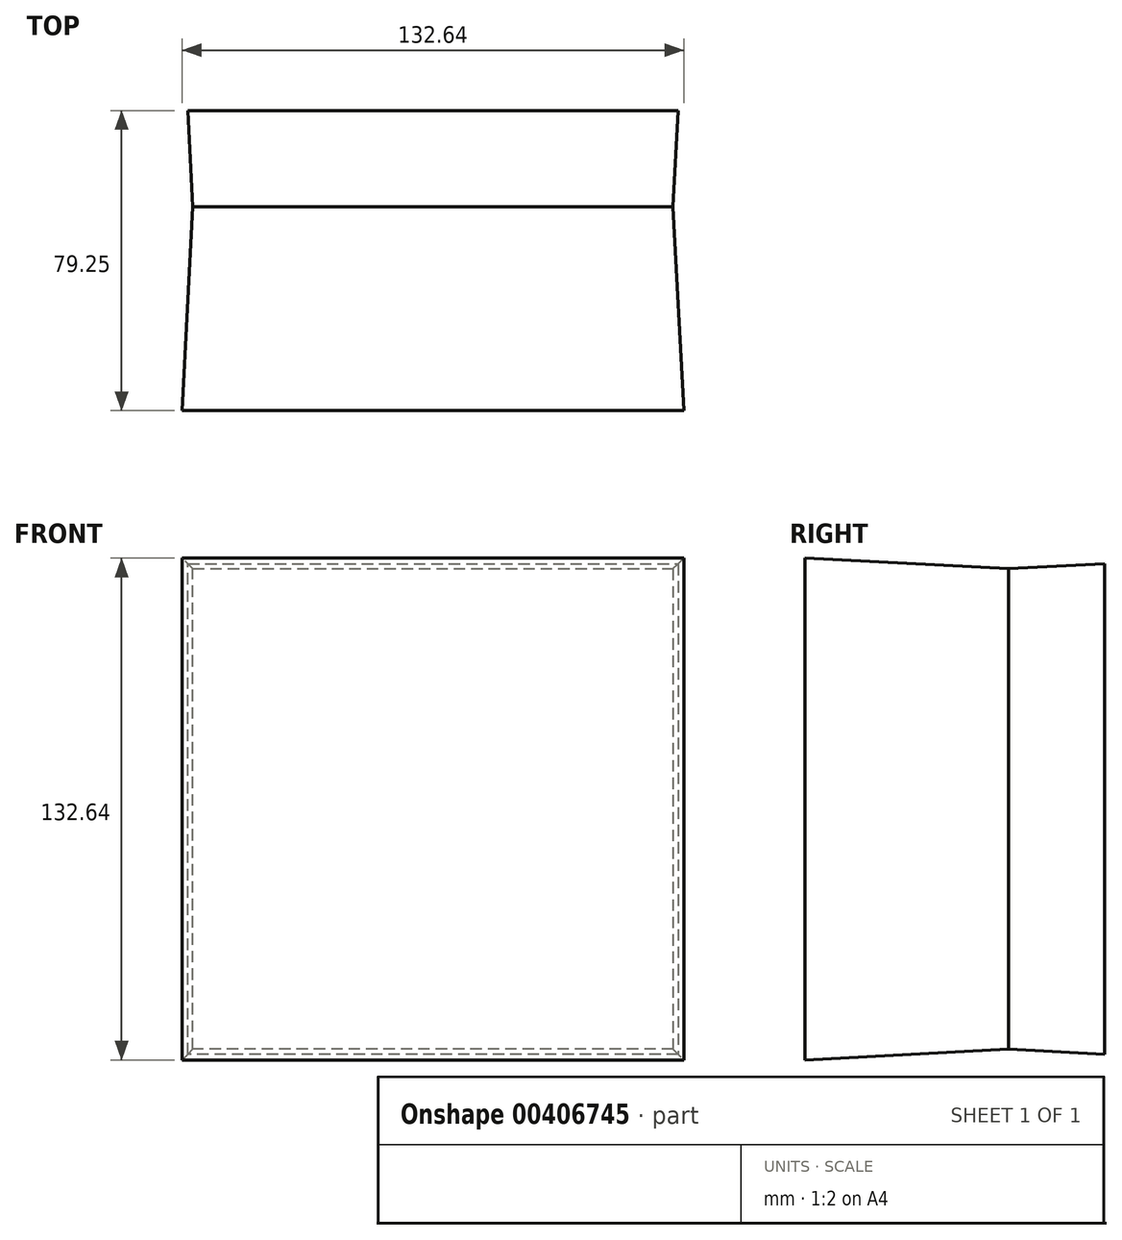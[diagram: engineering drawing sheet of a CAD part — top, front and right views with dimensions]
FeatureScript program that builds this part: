
annotation { "Feature Type Name" : "Feature", "Feature Type Description" : "" }
export const myFeature = defineFeature(function(context is Context, id is Id, definition is map)
    precondition{}
    {
        {
            var Q0;
            Q0=qCreatedBy(makeId("Front.planeOp"),FACE);
            var sketch = newSketch(context, id + "F0", { "sketchPlane" : qUnion([Q0])});
            skLineSegment(sketch, "E0.bottom", {"start": v(63.5, -63.5) * mm, "end": v(-63.5, -63.5) * mm});
            skLineSegment(sketch, "E0.top", {"start": v(63.5, 63.5) * mm, "end": v(-63.5, 63.5) * mm});
            skLineSegment(sketch, "E0.left", {"start": v(63.5, -63.5) * mm, "end": v(63.5, 63.5) * mm});
            skLineSegment(sketch, "E0.right", {"start": v(-63.5, -63.5) * mm, "end": v(-63.5, 63.5) * mm});
            skPoint(sketch, "E0.middle", {"position": v(0, 0) * mm});
            skSolve(sketch);
        }
        {
            var Q0;
            Q0=makeQuery(id+"F0.imprint","IMPRINT",FACE,{"disambiguationData":[TD([[makeQuery(id+"F0.imprint","IMPRINT",EDGE,{"derivedFrom":sQuery(id+"F0.wireOp",EDGE,"E0.bottom")}),-1.0]])]});
            extrude(context, id + "F1", {"entities" : qUnion([Q0]), "depth" : 53.85 * mm, "hasDraft" : true, "draftAngle" : 3 * degree, "hasSecondDirection" : true, "secondDirectionOppositeDirection" : true, "secondDirectionDepth" : 25.4 * mm, "hasSecondDirectionDraft" : true, "secondDirectionDraftAngle" : 3 * degree});
        }
    });
